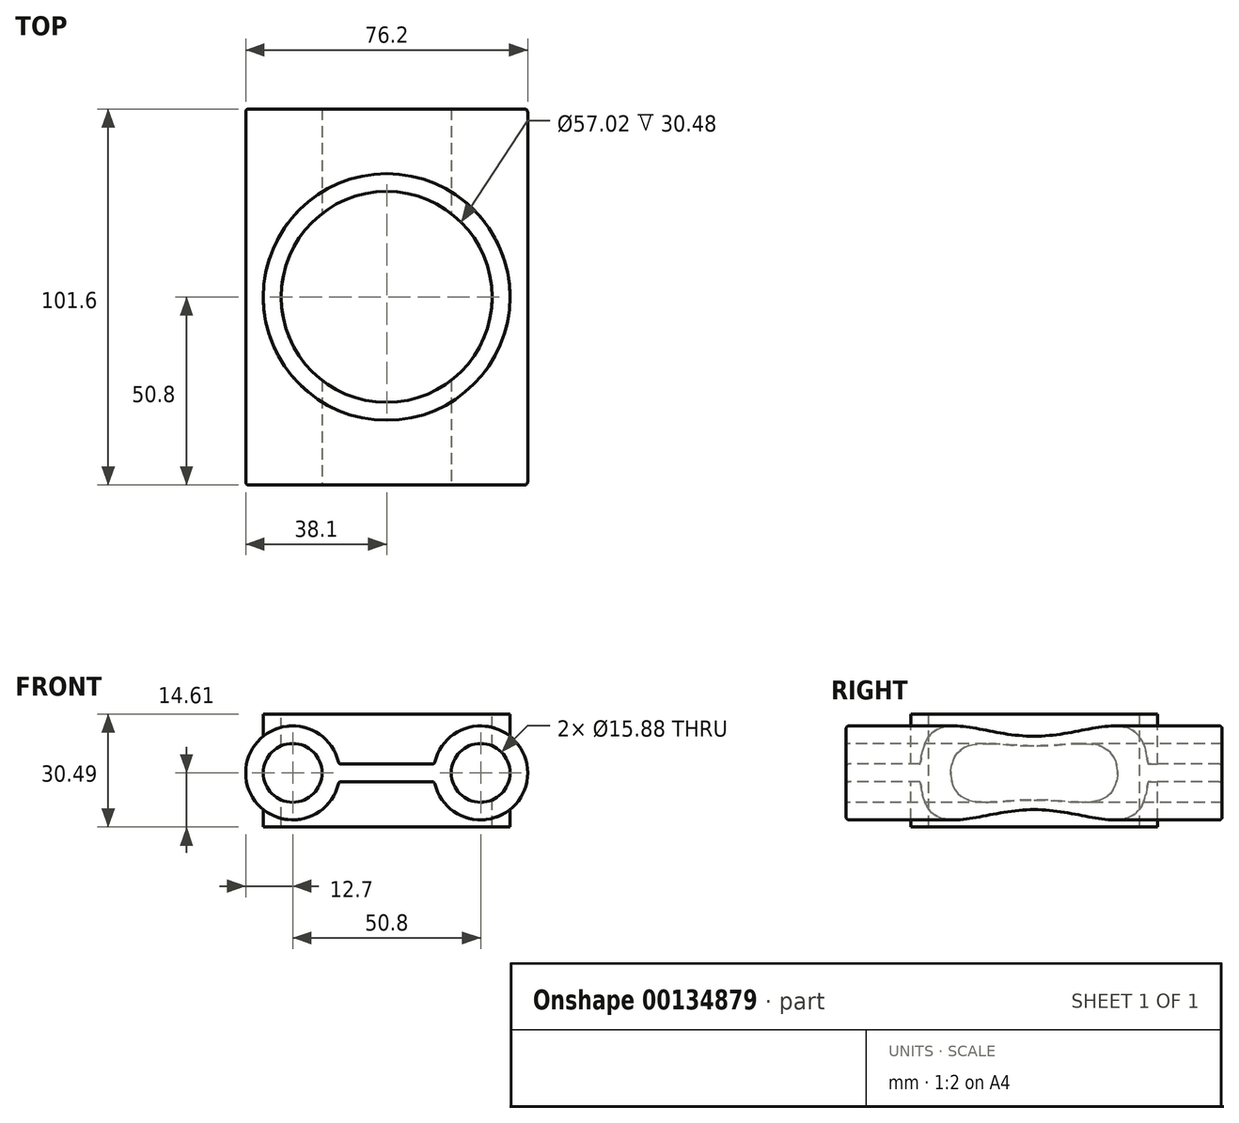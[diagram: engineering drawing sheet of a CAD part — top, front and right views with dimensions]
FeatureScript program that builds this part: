
annotation { "Feature Type Name" : "Feature", "Feature Type Description" : "" }
export const myFeature = defineFeature(function(context is Context, id is Id, definition is map)
    precondition{}
    {
        {
            var Q0;
            Q0=qCreatedBy(makeId("Front.planeOp"),FACE);
            var sketch = newSketch(context, id + "F0", { "sketchPlane" : qUnion([Q0])});
            skCircle(sketch, "E0", {"center": v(-25.4, 0) * mm, "radius": 7.94 * mm});
            skCircle(sketch, "E1", {"center": v(25.4, 0) * mm, "radius": 7.94 * mm});
            skLineSegment(sketch, "E2.bottom", {"start": v(-25.4, -12.7) * mm, "end": v(25.4, -12.7) * mm});
            skLineSegment(sketch, "E2.top", {"start": v(-25.4, 12.7) * mm, "end": v(25.4, 12.7) * mm});
            skLineSegment(sketch, "E3", {"start": v(0, 27.36) * mm, "end": v(0, -25.58) * mm, "construction": true});
            skArc(sketch, "E4.filletArc", {"start": v(-25.4, 12.7) * mm, "mid": v(-34.38, 8.98) * mm, "end": v(-38.1, 0) * mm});
            skLineSegment(sketch, "E5", {"start": v(41.42, 0) * mm, "end": v(-42.77, 0) * mm, "construction": true});
            skArc(sketch, "E6", {"start": v(25.4, -12.7) * mm, "mid": v(34.38, -8.98) * mm, "end": v(38.1, 0) * mm});
            skArc(sketch, "E7", {"start": v(25.4, 12.7) * mm, "mid": v(17.3, 9.79) * mm, "end": v(12.93, 2.38) * mm});
            skArc(sketch, "E8", {"start": v(-25.4, 12.7) * mm, "mid": v(-17.3, 9.79) * mm, "end": v(-12.93, 2.38) * mm});
            skLineSegment(sketch, "E9", {"start": v(12.93, 2.38) * mm, "end": v(-12.93, 2.38) * mm});
            skLineSegment(sketch, "E10", {"start": v(-12.93, -2.38) * mm, "end": v(12.93, -2.38) * mm});
            skArc(sketch, "E11.trimOffspring", {"start": v(-12.93, -2.38) * mm, "mid": v(-17.3, -9.79) * mm, "end": v(-25.4, -12.7) * mm});
            skArc(sketch, "E12.trimOffspring", {"start": v(12.93, -2.38) * mm, "mid": v(17.3, -9.79) * mm, "end": v(25.4, -12.7) * mm});
            skArc(sketch, "E13.trimOffspring", {"start": v(38.1, 0) * mm, "mid": v(34.38, 8.98) * mm, "end": v(25.4, 12.7) * mm});
            skArc(sketch, "E14.trimOffspring", {"start": v(-38.1, 0) * mm, "mid": v(-34.38, -8.98) * mm, "end": v(-25.4, -12.7) * mm});
            skLineSegment(sketch, "E15", {"start": v(-33.34, 24.61) * mm, "end": v(-33.34, -18.67) * mm, "construction": true});
            skSolve(sketch);
        }
        {
            var Q0;
            Q0=makeQuery(id+"F0.imprint","IMPRINT",FACE,{"disambiguationData":[TD([[makeQuery(id+"F0.imprint","IMPRINT",EDGE,{"derivedFrom":sQuery(id+"F0.wireOp",EDGE,"E0")}),-1.0]])]});
            var Q1;
            Q1=makeQuery(id+"F0.imprint","IMPRINT",FACE,{"disambiguationData":[TD([[makeQuery(id+"F0.imprint","IMPRINT",EDGE,{"derivedFrom":sQuery(id+"F0.wireOp",EDGE,"E0")}),1.0]])]});
            var Q2;
            Q2=makeQuery(id+"F0.imprint","IMPRINT",FACE,{"disambiguationData":[TD([[makeQuery(id+"F0.imprint","IMPRINT",EDGE,{"derivedFrom":sQuery(id+"F0.wireOp",EDGE,"E1")}),1.0]])]});
            extrude(context, id + "F1", {"entities" : qUnion([Q0, Q1, Q2]), "depth" : 101.6 * mm, "symmetric" : true});
        }
        {
            var Q0;
            Q0=qCreatedBy(makeId("Top.planeOp"),FACE);
            cPlane(context, id + "F2", {"entities" : qUnion([Q0]), "cplaneType" : CPlaneType.OFFSET, "offset" : 15.88 * mm, "width" : 152.4 * mm, "height" : 152.4 * mm});
        }
        {
            var Q0;
            Q0=qCreatedBy(makeId("Top.planeOp"),FACE);
            cPlane(context, id + "F3", {"entities" : qUnion([Q0]), "cplaneType" : CPlaneType.OFFSET, "offset" : 11.43 * mm, "oppositeDirection" : true, "width" : 152.4 * mm, "height" : 152.4 * mm});
        }
        {
            var Q0;
            Q0=qCreatedBy(id+"F2.planeOp",FACE);
            var sketch = newSketch(context, id + "F4", { "sketchPlane" : qUnion([Q0])});
            skCircle(sketch, "E16", {"center": v(0, 0) * mm, "radius": 33.34 * mm});
            skSolve(sketch);
        }
        {
            var Q0;
            Q0=qCreatedBy(id+"F3.planeOp",FACE);
            var sketch = newSketch(context, id + "F5", { "sketchPlane" : qUnion([Q0])});
            skLineSegment(sketch, "E17", {"start": v(0, -28.42) * mm, "end": v(0, -28.42) * mm, "construction": true});
            skPoint(sketch, "E17.startSnap0", {"position": v(0, -26.34) * mm});
            skPoint(sketch, "E17.endSnap0", {"position": v(0, -26.34) * mm});
            skLineSegment(sketch, "E18", {"start": v(0, -36.42) * mm, "end": v(0, 31.61) * mm, "construction": true});
            skCircle(sketch, "E19", {"center": v(0, 0) * mm, "radius": 27.94 * mm});
            skCircle(sketch, "E20", {"center": v(0, 0) * mm, "radius": 22.23 * mm});
            skSolve(sketch);
        }
        {
            var Q0;
            Q0=qCreatedBy(makeId("Front.planeOp"),FACE);
            var sketch = newSketch(context, id + "F6", { "sketchPlane" : qUnion([Q0])});
            skCircle(sketch, "E21", {"center": v(-25.4, 0) * mm, "radius": 7.94 * mm});
            skCircle(sketch, "E22", {"center": v(25.4, 0) * mm, "radius": 7.94 * mm});
            skSolve(sketch);
        }
        {
            var Q0;
            Q0=makeQuery(id+"F1.opExtrude","CAP_FACE",FACE,{"disambiguationData":[OSD([sQuery(id+"F0.wireOp",EDGE,"E0"),sQuery(id+"F0.wireOp",EDGE,"E1"),sQuery(id+"F0.wireOp",EDGE,"E4.filletArc"),sQuery(id+"F0.wireOp",EDGE,"E6"),sQuery(id+"F0.wireOp",EDGE,"E7"),sQuery(id+"F0.wireOp",EDGE,"E8"),sQuery(id+"F0.wireOp",EDGE,"E9"),sQuery(id+"F0.wireOp",EDGE,"E10"),sQuery(id+"F0.wireOp",EDGE,"E11.trimOffspring"),sQuery(id+"F0.wireOp",EDGE,"E12.trimOffspring"),sQuery(id+"F0.wireOp",EDGE,"56LLjDPh-25kw-j5da-6pGc-QQXyOrlAbZft"),sQuery(id+"F0.wireOp",EDGE,"nkBVuMIO-VIts-mmgG-adj7-daovQ4xWU2gD"),sQuery(id+"F0.wireOp",EDGE,"z16tnCEl-DL2h-uVAb-m06f-pflpMNFIArZW"),sQuery(id+"F0.wireOp",EDGE,"0xnEmYim-vQBw-8N55-9MmZ-LrTOjcDv7Glw"),sQuery(id+"F0.wireOp",EDGE,"68f398ec-cf93-4add-bcc9-37bf96ad6e88"),sQuery(id+"F0.wireOp",EDGE,"e56ac5f7-e3d4-4c3f-b5e2-56972c4acdce"),sQuery(id+"F0.wireOp",EDGE,"E13.trimOffspring"),sQuery(id+"F0.wireOp",EDGE,"E14.trimOffspring")])],"isStart":false});
            var Q1;
            Q1=makeQuery(id+"F1.opExtrude","CAP_EDGE",EDGE,{"disambiguationData":[OSD([sQuery(id+"F0.wireOp",EDGE,"E1")])],"isStart":true});
            var Q2;
            Q2=makeQuery(id+"F1.opExtrude","CAP_EDGE",EDGE,{"disambiguationData":[OSD([sQuery(id+"F0.wireOp",EDGE,"E0")])],"isStart":true});
            var Q3;
            Q3=makeQuery(id+"F1.opExtrude","CAP_FACE",FACE,{"disambiguationData":[OSD([sQuery(id+"F0.wireOp",EDGE,"E0"),sQuery(id+"F0.wireOp",EDGE,"E1"),sQuery(id+"F0.wireOp",EDGE,"E4.filletArc"),sQuery(id+"F0.wireOp",EDGE,"E6"),sQuery(id+"F0.wireOp",EDGE,"E7"),sQuery(id+"F0.wireOp",EDGE,"E8"),sQuery(id+"F0.wireOp",EDGE,"E9"),sQuery(id+"F0.wireOp",EDGE,"E10"),sQuery(id+"F0.wireOp",EDGE,"E11.trimOffspring"),sQuery(id+"F0.wireOp",EDGE,"E12.trimOffspring"),sQuery(id+"F0.wireOp",EDGE,"56LLjDPh-25kw-j5da-6pGc-QQXyOrlAbZft"),sQuery(id+"F0.wireOp",EDGE,"nkBVuMIO-VIts-mmgG-adj7-daovQ4xWU2gD"),sQuery(id+"F0.wireOp",EDGE,"z16tnCEl-DL2h-uVAb-m06f-pflpMNFIArZW"),sQuery(id+"F0.wireOp",EDGE,"0xnEmYim-vQBw-8N55-9MmZ-LrTOjcDv7Glw"),sQuery(id+"F0.wireOp",EDGE,"68f398ec-cf93-4add-bcc9-37bf96ad6e88"),sQuery(id+"F0.wireOp",EDGE,"e56ac5f7-e3d4-4c3f-b5e2-56972c4acdce"),sQuery(id+"F0.wireOp",EDGE,"E13.trimOffspring"),sQuery(id+"F0.wireOp",EDGE,"E14.trimOffspring")])],"isStart":true});
            var Q4;
            {var subQ0=sQuery(id+"F0.wireOp",EDGE,"E14.trimOffspring");var subQ1=sQuery(id+"F0.wireOp",EDGE,"E12.trimOffspring");var subQ2=sQuery(id+"F0.wireOp",EDGE,"E11.trimOffspring");var subQ3=sQuery(id+"F0.wireOp",EDGE,"E10");var subQ4=sQuery(id+"F0.wireOp",EDGE,"E6");Q4=makeQuery(id+"Fc4ntuCPbaOE7TT_1.boolean.opBoolean","INTERSECT",EDGE,{"derivedFrom":[makeQuery(id+"FMdS09tuQhoFYWg_1.boolean.opBoolean","SPLIT",FACE,{"disambiguationData":[TD([makeQuery(id+"F1.opExtrude","CAP_FACE",FACE,{"disambiguationData":[OSD([sQuery(id+"F0.wireOp",EDGE,"E0"),sQuery(id+"F0.wireOp",EDGE,"E1"),sQuery(id+"F0.wireOp",EDGE,"E4.filletArc"),subQ4,sQuery(id+"F0.wireOp",EDGE,"E7"),sQuery(id+"F0.wireOp",EDGE,"E8"),sQuery(id+"F0.wireOp",EDGE,"E9"),subQ3,subQ2,subQ1,sQuery(id+"F0.wireOp",EDGE,"56LLjDPh-25kw-j5da-6pGc-QQXyOrlAbZft"),sQuery(id+"F0.wireOp",EDGE,"nkBVuMIO-VIts-mmgG-adj7-daovQ4xWU2gD"),sQuery(id+"F0.wireOp",EDGE,"z16tnCEl-DL2h-uVAb-m06f-pflpMNFIArZW"),sQuery(id+"F0.wireOp",EDGE,"0xnEmYim-vQBw-8N55-9MmZ-LrTOjcDv7Glw"),sQuery(id+"F0.wireOp",EDGE,"68f398ec-cf93-4add-bcc9-37bf96ad6e88"),sQuery(id+"F0.wireOp",EDGE,"e56ac5f7-e3d4-4c3f-b5e2-56972c4acdce"),sQuery(id+"F0.wireOp",EDGE,"E13.trimOffspring"),subQ0])],"isStart":true})])],"derivedFrom":makeQuery(id+"F1.opExtrude","SWEPT_FACE",FACE,{"disambiguationData":[OSD([subQ3])]})}),makeQuery(id+"Fc4ntuCPbaOE7TT_1.opExtrude","SWEPT_FACE",FACE,{"disambiguationData":[OSD([sQuery(id+"F5.wireOp",EDGE,"E19")])]})]});}
            var Q5;
            {var subQ7=sQuery(id+"F0.wireOp",EDGE,"nkBVuMIO-VIts-mmgG-adj7-daovQ4xWU2gD");var subQ9=sQuery(id+"F0.wireOp",EDGE,"E12.trimOffspring");var subQ14=sQuery(id+"F0.wireOp",EDGE,"E6");Q5=makeQuery(id+"Fc4ntuCPbaOE7TT_1.boolean.opBoolean","INTERSECT",EDGE,{"disambiguationData":[OD(0.0)],"derivedFrom":[makeQuery(id+"FMdS09tuQhoFYWg_1.boolean.opBoolean","SPLIT",FACE,{"disambiguationData":[TD([makeQuery(id+"F1.opExtrude","SWEPT_FACE",FACE,{"disambiguationData":[OSD([subQ7])]})])],"derivedFrom":makeQuery(id+"F1.opExtrude","SWEPT_FACE",FACE,{"disambiguationData":[OSD([subQ14,subQ9])]})}),makeQuery(id+"Fc4ntuCPbaOE7TT_1.opExtrude","SWEPT_FACE",FACE,{"disambiguationData":[OSD([sQuery(id+"F5.wireOp",EDGE,"E19")])]})]});}
            var Q6;
            {var subQ0=sQuery(id+"F0.wireOp",EDGE,"0xnEmYim-vQBw-8N55-9MmZ-LrTOjcDv7Glw");var subQ1=sQuery(id+"F0.wireOp",EDGE,"E14.trimOffspring");var subQ9=sQuery(id+"F0.wireOp",EDGE,"E11.trimOffspring");Q6=makeQuery(id+"Fc4ntuCPbaOE7TT_1.boolean.opBoolean","INTERSECT",EDGE,{"disambiguationData":[OD(0.0)],"derivedFrom":[makeQuery(id+"FMdS09tuQhoFYWg_1.boolean.opBoolean","SPLIT",FACE,{"disambiguationData":[TD([makeQuery(id+"F1.opExtrude","SWEPT_FACE",FACE,{"disambiguationData":[OSD([subQ0])]})])],"derivedFrom":makeQuery(id+"F1.opExtrude","SWEPT_FACE",FACE,{"disambiguationData":[OSD([subQ9,subQ1])]})}),makeQuery(id+"Fc4ntuCPbaOE7TT_1.opExtrude","SWEPT_FACE",FACE,{"disambiguationData":[OSD([sQuery(id+"F5.wireOp",EDGE,"E19")])]})]});}
            var Q7;
            {var subQ7=sQuery(id+"F0.wireOp",EDGE,"nkBVuMIO-VIts-mmgG-adj7-daovQ4xWU2gD");var subQ9=sQuery(id+"F0.wireOp",EDGE,"E12.trimOffspring");var subQ14=sQuery(id+"F0.wireOp",EDGE,"E6");Q7=makeQuery(id+"Fc4ntuCPbaOE7TT_1.boolean.opBoolean","INTERSECT",EDGE,{"disambiguationData":[OD(1.0)],"derivedFrom":[makeQuery(id+"FMdS09tuQhoFYWg_1.boolean.opBoolean","SPLIT",FACE,{"disambiguationData":[TD([makeQuery(id+"F1.opExtrude","SWEPT_FACE",FACE,{"disambiguationData":[OSD([subQ7])]})])],"derivedFrom":makeQuery(id+"F1.opExtrude","SWEPT_FACE",FACE,{"disambiguationData":[OSD([subQ14,subQ9])]})}),makeQuery(id+"Fc4ntuCPbaOE7TT_1.opExtrude","SWEPT_FACE",FACE,{"disambiguationData":[OSD([sQuery(id+"F5.wireOp",EDGE,"E19")])]})]});}
            var Q8;
            {var subQ0=sQuery(id+"F0.wireOp",EDGE,"E14.trimOffspring");var subQ1=sQuery(id+"F0.wireOp",EDGE,"E12.trimOffspring");var subQ2=sQuery(id+"F0.wireOp",EDGE,"E11.trimOffspring");var subQ3=sQuery(id+"F0.wireOp",EDGE,"E10");var subQ4=sQuery(id+"F0.wireOp",EDGE,"E6");Q8=makeQuery(id+"Fc4ntuCPbaOE7TT_1.boolean.opBoolean","INTERSECT",EDGE,{"derivedFrom":[makeQuery(id+"FMdS09tuQhoFYWg_1.boolean.opBoolean","SPLIT",FACE,{"disambiguationData":[TD([makeQuery(id+"F1.opExtrude","CAP_FACE",FACE,{"disambiguationData":[OSD([sQuery(id+"F0.wireOp",EDGE,"E0"),sQuery(id+"F0.wireOp",EDGE,"E1"),sQuery(id+"F0.wireOp",EDGE,"E4.filletArc"),subQ4,sQuery(id+"F0.wireOp",EDGE,"E7"),sQuery(id+"F0.wireOp",EDGE,"E8"),sQuery(id+"F0.wireOp",EDGE,"E9"),subQ3,subQ2,subQ1,sQuery(id+"F0.wireOp",EDGE,"56LLjDPh-25kw-j5da-6pGc-QQXyOrlAbZft"),sQuery(id+"F0.wireOp",EDGE,"nkBVuMIO-VIts-mmgG-adj7-daovQ4xWU2gD"),sQuery(id+"F0.wireOp",EDGE,"z16tnCEl-DL2h-uVAb-m06f-pflpMNFIArZW"),sQuery(id+"F0.wireOp",EDGE,"0xnEmYim-vQBw-8N55-9MmZ-LrTOjcDv7Glw"),sQuery(id+"F0.wireOp",EDGE,"68f398ec-cf93-4add-bcc9-37bf96ad6e88"),sQuery(id+"F0.wireOp",EDGE,"e56ac5f7-e3d4-4c3f-b5e2-56972c4acdce"),sQuery(id+"F0.wireOp",EDGE,"E13.trimOffspring"),subQ0])],"isStart":false})])],"derivedFrom":makeQuery(id+"F1.opExtrude","SWEPT_FACE",FACE,{"disambiguationData":[OSD([subQ3])]})}),makeQuery(id+"Fc4ntuCPbaOE7TT_1.opExtrude","SWEPT_FACE",FACE,{"disambiguationData":[OSD([sQuery(id+"F5.wireOp",EDGE,"E19")])]})]});}
            var Q9;
            {var subQ0=sQuery(id+"F0.wireOp",EDGE,"0xnEmYim-vQBw-8N55-9MmZ-LrTOjcDv7Glw");var subQ1=sQuery(id+"F0.wireOp",EDGE,"E14.trimOffspring");var subQ9=sQuery(id+"F0.wireOp",EDGE,"E11.trimOffspring");Q9=makeQuery(id+"Fc4ntuCPbaOE7TT_1.boolean.opBoolean","INTERSECT",EDGE,{"disambiguationData":[OD(1.0)],"derivedFrom":[makeQuery(id+"FMdS09tuQhoFYWg_1.boolean.opBoolean","SPLIT",FACE,{"disambiguationData":[TD([makeQuery(id+"F1.opExtrude","SWEPT_FACE",FACE,{"disambiguationData":[OSD([subQ0])]})])],"derivedFrom":makeQuery(id+"F1.opExtrude","SWEPT_FACE",FACE,{"disambiguationData":[OSD([subQ9,subQ1])]})}),makeQuery(id+"Fc4ntuCPbaOE7TT_1.opExtrude","SWEPT_FACE",FACE,{"disambiguationData":[OSD([sQuery(id+"F5.wireOp",EDGE,"E19")])]})]});}
            var Q10;
            Q10=makeQuery(id+"FTNQrZDtOkg16al_1.opExtrude","TWEAK_EDGE",EDGE,{"disambiguationData":[OD(0.0)],"derivedFrom":[makeQuery(id+"F1.opExtrude","SWEPT_FACE",FACE,{"disambiguationData":[OSD([sQuery(id+"F0.wireOp",EDGE,"E9")])]}),makeQuery(id+"F4.imprint","IMPRINT",EDGE,{"derivedFrom":sQuery(id+"F4.wireOp",EDGE,"E16")})]});
            var Q11;
            Q11=makeQuery(id+"FTNQrZDtOkg16al_1.opExtrude","TWEAK_EDGE",EDGE,{"derivedFrom":[makeQuery(id+"F1.opExtrude","SWEPT_FACE",FACE,{"disambiguationData":[OSD([sQuery(id+"F0.wireOp",EDGE,"56LLjDPh-25kw-j5da-6pGc-QQXyOrlAbZft")])]}),makeQuery(id+"F4.imprint","IMPRINT",EDGE,{"derivedFrom":sQuery(id+"F4.wireOp",EDGE,"E16")})]});
            var Q12;
            Q12=makeQuery(id+"FTNQrZDtOkg16al_1.opExtrude","TWEAK_EDGE",EDGE,{"derivedFrom":[makeQuery(id+"F1.opExtrude","SWEPT_FACE",FACE,{"disambiguationData":[OSD([sQuery(id+"F0.wireOp",EDGE,"z16tnCEl-DL2h-uVAb-m06f-pflpMNFIArZW")])]}),makeQuery(id+"F4.imprint","IMPRINT",EDGE,{"derivedFrom":sQuery(id+"F4.wireOp",EDGE,"E16")})]});
            var Q13;
            Q13=makeQuery(id+"FTNQrZDtOkg16al_1.opExtrude","TWEAK_EDGE",EDGE,{"disambiguationData":[OD(1.0)],"derivedFrom":[makeQuery(id+"F1.opExtrude","SWEPT_FACE",FACE,{"disambiguationData":[OSD([sQuery(id+"F0.wireOp",EDGE,"E9")])]}),makeQuery(id+"F4.imprint","IMPRINT",EDGE,{"derivedFrom":sQuery(id+"F4.wireOp",EDGE,"E16")})]});
            var Q14;
            Q14=makeQuery(id+"F1.opExtrude","SWEPT_EDGE",EDGE,{"disambiguationData":[OSD([sQuery(id+"F0.wireOp",EDGE,"E6"),sQuery(id+"F0.wireOp",EDGE,"nkBVuMIO-VIts-mmgG-adj7-daovQ4xWU2gD")])]});
            var Q15;
            Q15=makeQuery(id+"F1.opExtrude","SWEPT_EDGE",EDGE,{"disambiguationData":[OSD([sQuery(id+"F0.wireOp",EDGE,"0xnEmYim-vQBw-8N55-9MmZ-LrTOjcDv7Glw"),sQuery(id+"F0.wireOp",EDGE,"E14.trimOffspring")])]});
            var Q16;
            {var subQ0=sQuery(id+"F0.wireOp",EDGE,"E14.trimOffspring");var subQ1=sQuery(id+"F0.wireOp",EDGE,"E11.trimOffspring");var subQ2=sQuery(id+"F0.wireOp",EDGE,"E10");Q16=makeQuery(id+"FMdS09tuQhoFYWg_1.boolean.opBoolean","SPLIT",EDGE,{"disambiguationData":[TD([makeQuery(id+"F1.opExtrude","CAP_FACE",FACE,{"disambiguationData":[OSD([sQuery(id+"F0.wireOp",EDGE,"E0"),sQuery(id+"F0.wireOp",EDGE,"E1"),sQuery(id+"F0.wireOp",EDGE,"E4.filletArc"),sQuery(id+"F0.wireOp",EDGE,"E6"),sQuery(id+"F0.wireOp",EDGE,"E7"),sQuery(id+"F0.wireOp",EDGE,"E8"),sQuery(id+"F0.wireOp",EDGE,"E9"),subQ2,subQ1,sQuery(id+"F0.wireOp",EDGE,"E12.trimOffspring"),sQuery(id+"F0.wireOp",EDGE,"56LLjDPh-25kw-j5da-6pGc-QQXyOrlAbZft"),sQuery(id+"F0.wireOp",EDGE,"nkBVuMIO-VIts-mmgG-adj7-daovQ4xWU2gD"),sQuery(id+"F0.wireOp",EDGE,"z16tnCEl-DL2h-uVAb-m06f-pflpMNFIArZW"),sQuery(id+"F0.wireOp",EDGE,"0xnEmYim-vQBw-8N55-9MmZ-LrTOjcDv7Glw"),sQuery(id+"F0.wireOp",EDGE,"68f398ec-cf93-4add-bcc9-37bf96ad6e88"),sQuery(id+"F0.wireOp",EDGE,"e56ac5f7-e3d4-4c3f-b5e2-56972c4acdce"),sQuery(id+"F0.wireOp",EDGE,"E13.trimOffspring"),subQ0])],"isStart":true})])],"derivedFrom":makeQuery(id+"F1.opExtrude","SWEPT_EDGE",EDGE,{"disambiguationData":[OSD([subQ2,subQ1])]})});}
            var Q17;
            {var subQ0=sQuery(id+"F0.wireOp",EDGE,"E14.trimOffspring");var subQ1=sQuery(id+"F0.wireOp",EDGE,"E11.trimOffspring");var subQ2=sQuery(id+"F0.wireOp",EDGE,"E10");Q17=makeQuery(id+"FMdS09tuQhoFYWg_1.boolean.opBoolean","SPLIT",EDGE,{"disambiguationData":[TD([makeQuery(id+"F1.opExtrude","CAP_FACE",FACE,{"disambiguationData":[OSD([sQuery(id+"F0.wireOp",EDGE,"E0"),sQuery(id+"F0.wireOp",EDGE,"E1"),sQuery(id+"F0.wireOp",EDGE,"E4.filletArc"),sQuery(id+"F0.wireOp",EDGE,"E6"),sQuery(id+"F0.wireOp",EDGE,"E7"),sQuery(id+"F0.wireOp",EDGE,"E8"),sQuery(id+"F0.wireOp",EDGE,"E9"),subQ2,subQ1,sQuery(id+"F0.wireOp",EDGE,"E12.trimOffspring"),sQuery(id+"F0.wireOp",EDGE,"56LLjDPh-25kw-j5da-6pGc-QQXyOrlAbZft"),sQuery(id+"F0.wireOp",EDGE,"nkBVuMIO-VIts-mmgG-adj7-daovQ4xWU2gD"),sQuery(id+"F0.wireOp",EDGE,"z16tnCEl-DL2h-uVAb-m06f-pflpMNFIArZW"),sQuery(id+"F0.wireOp",EDGE,"0xnEmYim-vQBw-8N55-9MmZ-LrTOjcDv7Glw"),sQuery(id+"F0.wireOp",EDGE,"68f398ec-cf93-4add-bcc9-37bf96ad6e88"),sQuery(id+"F0.wireOp",EDGE,"e56ac5f7-e3d4-4c3f-b5e2-56972c4acdce"),sQuery(id+"F0.wireOp",EDGE,"E13.trimOffspring"),subQ0])],"isStart":false})])],"derivedFrom":makeQuery(id+"F1.opExtrude","SWEPT_EDGE",EDGE,{"disambiguationData":[OSD([subQ2,subQ1])]})});}
            var Q18;
            {var subQ0=sQuery(id+"F0.wireOp",EDGE,"E12.trimOffspring");var subQ1=sQuery(id+"F0.wireOp",EDGE,"E10");var subQ2=sQuery(id+"F0.wireOp",EDGE,"E6");Q18=makeQuery(id+"FMdS09tuQhoFYWg_1.boolean.opBoolean","SPLIT",EDGE,{"disambiguationData":[TD([makeQuery(id+"F1.opExtrude","CAP_FACE",FACE,{"disambiguationData":[OSD([sQuery(id+"F0.wireOp",EDGE,"E0"),sQuery(id+"F0.wireOp",EDGE,"E1"),sQuery(id+"F0.wireOp",EDGE,"E4.filletArc"),subQ2,sQuery(id+"F0.wireOp",EDGE,"E7"),sQuery(id+"F0.wireOp",EDGE,"E8"),sQuery(id+"F0.wireOp",EDGE,"E9"),subQ1,sQuery(id+"F0.wireOp",EDGE,"E11.trimOffspring"),subQ0,sQuery(id+"F0.wireOp",EDGE,"56LLjDPh-25kw-j5da-6pGc-QQXyOrlAbZft"),sQuery(id+"F0.wireOp",EDGE,"nkBVuMIO-VIts-mmgG-adj7-daovQ4xWU2gD"),sQuery(id+"F0.wireOp",EDGE,"z16tnCEl-DL2h-uVAb-m06f-pflpMNFIArZW"),sQuery(id+"F0.wireOp",EDGE,"0xnEmYim-vQBw-8N55-9MmZ-LrTOjcDv7Glw"),sQuery(id+"F0.wireOp",EDGE,"68f398ec-cf93-4add-bcc9-37bf96ad6e88"),sQuery(id+"F0.wireOp",EDGE,"e56ac5f7-e3d4-4c3f-b5e2-56972c4acdce"),sQuery(id+"F0.wireOp",EDGE,"E13.trimOffspring"),sQuery(id+"F0.wireOp",EDGE,"E14.trimOffspring")])],"isStart":true})])],"derivedFrom":makeQuery(id+"F1.opExtrude","SWEPT_EDGE",EDGE,{"disambiguationData":[OSD([subQ1,subQ0])]})});}
            var Q19;
            {var subQ0=sQuery(id+"F0.wireOp",EDGE,"E12.trimOffspring");var subQ1=sQuery(id+"F0.wireOp",EDGE,"E10");var subQ2=sQuery(id+"F0.wireOp",EDGE,"E6");Q19=makeQuery(id+"FMdS09tuQhoFYWg_1.boolean.opBoolean","SPLIT",EDGE,{"disambiguationData":[TD([makeQuery(id+"F1.opExtrude","CAP_FACE",FACE,{"disambiguationData":[OSD([sQuery(id+"F0.wireOp",EDGE,"E0"),sQuery(id+"F0.wireOp",EDGE,"E1"),sQuery(id+"F0.wireOp",EDGE,"E4.filletArc"),subQ2,sQuery(id+"F0.wireOp",EDGE,"E7"),sQuery(id+"F0.wireOp",EDGE,"E8"),sQuery(id+"F0.wireOp",EDGE,"E9"),subQ1,sQuery(id+"F0.wireOp",EDGE,"E11.trimOffspring"),subQ0,sQuery(id+"F0.wireOp",EDGE,"56LLjDPh-25kw-j5da-6pGc-QQXyOrlAbZft"),sQuery(id+"F0.wireOp",EDGE,"nkBVuMIO-VIts-mmgG-adj7-daovQ4xWU2gD"),sQuery(id+"F0.wireOp",EDGE,"z16tnCEl-DL2h-uVAb-m06f-pflpMNFIArZW"),sQuery(id+"F0.wireOp",EDGE,"0xnEmYim-vQBw-8N55-9MmZ-LrTOjcDv7Glw"),sQuery(id+"F0.wireOp",EDGE,"68f398ec-cf93-4add-bcc9-37bf96ad6e88"),sQuery(id+"F0.wireOp",EDGE,"e56ac5f7-e3d4-4c3f-b5e2-56972c4acdce"),sQuery(id+"F0.wireOp",EDGE,"E13.trimOffspring"),sQuery(id+"F0.wireOp",EDGE,"E14.trimOffspring")])],"isStart":false})])],"derivedFrom":makeQuery(id+"F1.opExtrude","SWEPT_EDGE",EDGE,{"disambiguationData":[OSD([subQ1,subQ0])]})});}
            var Q20;
            {var subQ0=sQuery(id+"F0.wireOp",EDGE,"z16tnCEl-DL2h-uVAb-m06f-pflpMNFIArZW");var subQ1=sQuery(id+"F0.wireOp",EDGE,"E8");var subQ2=sQuery(id+"F0.wireOp",EDGE,"E4.filletArc");Q20=makeQuery(id+"FTNQrZDtOkg16al_1.boolean.opBoolean","SPLIT",EDGE,{"disambiguationData":[TD([makeQuery(id+"F1.opExtrude","CAP_FACE",FACE,{"disambiguationData":[OSD([sQuery(id+"F0.wireOp",EDGE,"E0"),sQuery(id+"F0.wireOp",EDGE,"E1"),subQ2,sQuery(id+"F0.wireOp",EDGE,"E6"),sQuery(id+"F0.wireOp",EDGE,"E7"),subQ1,sQuery(id+"F0.wireOp",EDGE,"E9"),sQuery(id+"F0.wireOp",EDGE,"E10"),sQuery(id+"F0.wireOp",EDGE,"E11.trimOffspring"),sQuery(id+"F0.wireOp",EDGE,"E12.trimOffspring"),sQuery(id+"F0.wireOp",EDGE,"56LLjDPh-25kw-j5da-6pGc-QQXyOrlAbZft"),sQuery(id+"F0.wireOp",EDGE,"nkBVuMIO-VIts-mmgG-adj7-daovQ4xWU2gD"),subQ0,sQuery(id+"F0.wireOp",EDGE,"0xnEmYim-vQBw-8N55-9MmZ-LrTOjcDv7Glw"),sQuery(id+"F0.wireOp",EDGE,"68f398ec-cf93-4add-bcc9-37bf96ad6e88"),sQuery(id+"F0.wireOp",EDGE,"e56ac5f7-e3d4-4c3f-b5e2-56972c4acdce"),sQuery(id+"F0.wireOp",EDGE,"E13.trimOffspring"),sQuery(id+"F0.wireOp",EDGE,"E14.trimOffspring")])],"isStart":false})])],"derivedFrom":makeQuery(id+"F1.opExtrude","SWEPT_EDGE",EDGE,{"disambiguationData":[OSD([subQ2,subQ0])]})});}
            var Q21;
            {var subQ0=sQuery(id+"F0.wireOp",EDGE,"z16tnCEl-DL2h-uVAb-m06f-pflpMNFIArZW");var subQ1=sQuery(id+"F0.wireOp",EDGE,"E8");var subQ2=sQuery(id+"F0.wireOp",EDGE,"E4.filletArc");Q21=makeQuery(id+"FTNQrZDtOkg16al_1.boolean.opBoolean","SPLIT",EDGE,{"disambiguationData":[TD([makeQuery(id+"F1.opExtrude","CAP_FACE",FACE,{"disambiguationData":[OSD([sQuery(id+"F0.wireOp",EDGE,"E0"),sQuery(id+"F0.wireOp",EDGE,"E1"),subQ2,sQuery(id+"F0.wireOp",EDGE,"E6"),sQuery(id+"F0.wireOp",EDGE,"E7"),subQ1,sQuery(id+"F0.wireOp",EDGE,"E9"),sQuery(id+"F0.wireOp",EDGE,"E10"),sQuery(id+"F0.wireOp",EDGE,"E11.trimOffspring"),sQuery(id+"F0.wireOp",EDGE,"E12.trimOffspring"),sQuery(id+"F0.wireOp",EDGE,"56LLjDPh-25kw-j5da-6pGc-QQXyOrlAbZft"),sQuery(id+"F0.wireOp",EDGE,"nkBVuMIO-VIts-mmgG-adj7-daovQ4xWU2gD"),subQ0,sQuery(id+"F0.wireOp",EDGE,"0xnEmYim-vQBw-8N55-9MmZ-LrTOjcDv7Glw"),sQuery(id+"F0.wireOp",EDGE,"68f398ec-cf93-4add-bcc9-37bf96ad6e88"),sQuery(id+"F0.wireOp",EDGE,"e56ac5f7-e3d4-4c3f-b5e2-56972c4acdce"),sQuery(id+"F0.wireOp",EDGE,"E13.trimOffspring"),sQuery(id+"F0.wireOp",EDGE,"E14.trimOffspring")])],"isStart":true})])],"derivedFrom":makeQuery(id+"F1.opExtrude","SWEPT_EDGE",EDGE,{"disambiguationData":[OSD([subQ2,subQ0])]})});}
            var Q22;
            {var subQ0=sQuery(id+"F0.wireOp",EDGE,"E9");var subQ1=sQuery(id+"F0.wireOp",EDGE,"E8");var subQ2=sQuery(id+"F0.wireOp",EDGE,"E4.filletArc");Q22=makeQuery(id+"FTNQrZDtOkg16al_1.boolean.opBoolean","SPLIT",EDGE,{"disambiguationData":[TD([makeQuery(id+"F1.opExtrude","CAP_FACE",FACE,{"disambiguationData":[OSD([sQuery(id+"F0.wireOp",EDGE,"E0"),sQuery(id+"F0.wireOp",EDGE,"E1"),subQ2,sQuery(id+"F0.wireOp",EDGE,"E6"),sQuery(id+"F0.wireOp",EDGE,"E7"),subQ1,subQ0,sQuery(id+"F0.wireOp",EDGE,"E10"),sQuery(id+"F0.wireOp",EDGE,"E11.trimOffspring"),sQuery(id+"F0.wireOp",EDGE,"E12.trimOffspring"),sQuery(id+"F0.wireOp",EDGE,"56LLjDPh-25kw-j5da-6pGc-QQXyOrlAbZft"),sQuery(id+"F0.wireOp",EDGE,"nkBVuMIO-VIts-mmgG-adj7-daovQ4xWU2gD"),sQuery(id+"F0.wireOp",EDGE,"z16tnCEl-DL2h-uVAb-m06f-pflpMNFIArZW"),sQuery(id+"F0.wireOp",EDGE,"0xnEmYim-vQBw-8N55-9MmZ-LrTOjcDv7Glw"),sQuery(id+"F0.wireOp",EDGE,"68f398ec-cf93-4add-bcc9-37bf96ad6e88"),sQuery(id+"F0.wireOp",EDGE,"e56ac5f7-e3d4-4c3f-b5e2-56972c4acdce"),sQuery(id+"F0.wireOp",EDGE,"E13.trimOffspring"),sQuery(id+"F0.wireOp",EDGE,"E14.trimOffspring")])],"isStart":true})])],"derivedFrom":makeQuery(id+"F1.opExtrude","SWEPT_EDGE",EDGE,{"disambiguationData":[OSD([subQ1,subQ0])]})});}
            var Q23;
            {var subQ0=sQuery(id+"F0.wireOp",EDGE,"E13.trimOffspring");var subQ1=sQuery(id+"F0.wireOp",EDGE,"E9");var subQ2=sQuery(id+"F0.wireOp",EDGE,"E7");Q23=makeQuery(id+"FTNQrZDtOkg16al_1.boolean.opBoolean","SPLIT",EDGE,{"disambiguationData":[TD([makeQuery(id+"F1.opExtrude","CAP_FACE",FACE,{"disambiguationData":[OSD([sQuery(id+"F0.wireOp",EDGE,"E0"),sQuery(id+"F0.wireOp",EDGE,"E1"),sQuery(id+"F0.wireOp",EDGE,"E4.filletArc"),sQuery(id+"F0.wireOp",EDGE,"E6"),subQ2,sQuery(id+"F0.wireOp",EDGE,"E8"),subQ1,sQuery(id+"F0.wireOp",EDGE,"E10"),sQuery(id+"F0.wireOp",EDGE,"E11.trimOffspring"),sQuery(id+"F0.wireOp",EDGE,"E12.trimOffspring"),sQuery(id+"F0.wireOp",EDGE,"56LLjDPh-25kw-j5da-6pGc-QQXyOrlAbZft"),sQuery(id+"F0.wireOp",EDGE,"nkBVuMIO-VIts-mmgG-adj7-daovQ4xWU2gD"),sQuery(id+"F0.wireOp",EDGE,"z16tnCEl-DL2h-uVAb-m06f-pflpMNFIArZW"),sQuery(id+"F0.wireOp",EDGE,"0xnEmYim-vQBw-8N55-9MmZ-LrTOjcDv7Glw"),sQuery(id+"F0.wireOp",EDGE,"68f398ec-cf93-4add-bcc9-37bf96ad6e88"),sQuery(id+"F0.wireOp",EDGE,"e56ac5f7-e3d4-4c3f-b5e2-56972c4acdce"),subQ0,sQuery(id+"F0.wireOp",EDGE,"E14.trimOffspring")])],"isStart":true})])],"derivedFrom":makeQuery(id+"F1.opExtrude","SWEPT_EDGE",EDGE,{"disambiguationData":[OSD([subQ2,subQ1])]})});}
            var Q24;
            {var subQ0=sQuery(id+"F0.wireOp",EDGE,"E13.trimOffspring");var subQ1=sQuery(id+"F0.wireOp",EDGE,"56LLjDPh-25kw-j5da-6pGc-QQXyOrlAbZft");var subQ2=sQuery(id+"F0.wireOp",EDGE,"E7");Q24=makeQuery(id+"FTNQrZDtOkg16al_1.boolean.opBoolean","SPLIT",EDGE,{"disambiguationData":[TD([makeQuery(id+"F1.opExtrude","CAP_FACE",FACE,{"disambiguationData":[OSD([sQuery(id+"F0.wireOp",EDGE,"E0"),sQuery(id+"F0.wireOp",EDGE,"E1"),sQuery(id+"F0.wireOp",EDGE,"E4.filletArc"),sQuery(id+"F0.wireOp",EDGE,"E6"),subQ2,sQuery(id+"F0.wireOp",EDGE,"E8"),sQuery(id+"F0.wireOp",EDGE,"E9"),sQuery(id+"F0.wireOp",EDGE,"E10"),sQuery(id+"F0.wireOp",EDGE,"E11.trimOffspring"),sQuery(id+"F0.wireOp",EDGE,"E12.trimOffspring"),subQ1,sQuery(id+"F0.wireOp",EDGE,"nkBVuMIO-VIts-mmgG-adj7-daovQ4xWU2gD"),sQuery(id+"F0.wireOp",EDGE,"z16tnCEl-DL2h-uVAb-m06f-pflpMNFIArZW"),sQuery(id+"F0.wireOp",EDGE,"0xnEmYim-vQBw-8N55-9MmZ-LrTOjcDv7Glw"),sQuery(id+"F0.wireOp",EDGE,"68f398ec-cf93-4add-bcc9-37bf96ad6e88"),sQuery(id+"F0.wireOp",EDGE,"e56ac5f7-e3d4-4c3f-b5e2-56972c4acdce"),subQ0,sQuery(id+"F0.wireOp",EDGE,"E14.trimOffspring")])],"isStart":true})])],"derivedFrom":makeQuery(id+"F1.opExtrude","SWEPT_EDGE",EDGE,{"disambiguationData":[OSD([subQ1,subQ0])]})});}
            var Q25;
            {var subQ0=sQuery(id+"F0.wireOp",EDGE,"E13.trimOffspring");var subQ1=sQuery(id+"F0.wireOp",EDGE,"56LLjDPh-25kw-j5da-6pGc-QQXyOrlAbZft");var subQ2=sQuery(id+"F0.wireOp",EDGE,"E7");Q25=makeQuery(id+"FTNQrZDtOkg16al_1.boolean.opBoolean","SPLIT",EDGE,{"disambiguationData":[TD([makeQuery(id+"F1.opExtrude","CAP_FACE",FACE,{"disambiguationData":[OSD([sQuery(id+"F0.wireOp",EDGE,"E0"),sQuery(id+"F0.wireOp",EDGE,"E1"),sQuery(id+"F0.wireOp",EDGE,"E4.filletArc"),sQuery(id+"F0.wireOp",EDGE,"E6"),subQ2,sQuery(id+"F0.wireOp",EDGE,"E8"),sQuery(id+"F0.wireOp",EDGE,"E9"),sQuery(id+"F0.wireOp",EDGE,"E10"),sQuery(id+"F0.wireOp",EDGE,"E11.trimOffspring"),sQuery(id+"F0.wireOp",EDGE,"E12.trimOffspring"),subQ1,sQuery(id+"F0.wireOp",EDGE,"nkBVuMIO-VIts-mmgG-adj7-daovQ4xWU2gD"),sQuery(id+"F0.wireOp",EDGE,"z16tnCEl-DL2h-uVAb-m06f-pflpMNFIArZW"),sQuery(id+"F0.wireOp",EDGE,"0xnEmYim-vQBw-8N55-9MmZ-LrTOjcDv7Glw"),sQuery(id+"F0.wireOp",EDGE,"68f398ec-cf93-4add-bcc9-37bf96ad6e88"),sQuery(id+"F0.wireOp",EDGE,"e56ac5f7-e3d4-4c3f-b5e2-56972c4acdce"),subQ0,sQuery(id+"F0.wireOp",EDGE,"E14.trimOffspring")])],"isStart":false})])],"derivedFrom":makeQuery(id+"F1.opExtrude","SWEPT_EDGE",EDGE,{"disambiguationData":[OSD([subQ1,subQ0])]})});}
            var Q26;
            Q26=makeQuery(id+"FTNQrZDtOkg16al_1.opExtrude","TWEAK_EDGE",EDGE,{"disambiguationData":[OD(1.0)],"derivedFrom":[makeQuery(id+"F1.opExtrude","SWEPT_FACE",FACE,{"disambiguationData":[OSD([sQuery(id+"F0.wireOp",EDGE,"E7"),sQuery(id+"F0.wireOp",EDGE,"E13.trimOffspring")])]}),makeQuery(id+"F4.imprint","IMPRINT",EDGE,{"derivedFrom":sQuery(id+"F4.wireOp",EDGE,"E16")})]});
            var Q27;
            Q27=makeQuery(id+"FTNQrZDtOkg16al_1.opExtrude","TWEAK_EDGE",EDGE,{"disambiguationData":[OD(1.0)],"derivedFrom":[makeQuery(id+"F1.opExtrude","SWEPT_FACE",FACE,{"disambiguationData":[OSD([sQuery(id+"F0.wireOp",EDGE,"E4.filletArc"),sQuery(id+"F0.wireOp",EDGE,"E8")])]}),makeQuery(id+"F4.imprint","IMPRINT",EDGE,{"derivedFrom":sQuery(id+"F4.wireOp",EDGE,"E16")})]});
            var Q28;
            Q28=makeQuery(id+"FTNQrZDtOkg16al_1.opExtrude","TWEAK_EDGE",EDGE,{"disambiguationData":[OD(0.0)],"derivedFrom":[makeQuery(id+"F1.opExtrude","SWEPT_FACE",FACE,{"disambiguationData":[OSD([sQuery(id+"F0.wireOp",EDGE,"E4.filletArc"),sQuery(id+"F0.wireOp",EDGE,"E8")])]}),makeQuery(id+"F4.imprint","IMPRINT",EDGE,{"derivedFrom":sQuery(id+"F4.wireOp",EDGE,"E16")})]});
            var Q29;
            Q29=makeQuery(id+"FTNQrZDtOkg16al_1.opExtrude","TWEAK_EDGE",EDGE,{"disambiguationData":[OD(0.0)],"derivedFrom":[makeQuery(id+"F1.opExtrude","SWEPT_FACE",FACE,{"disambiguationData":[OSD([sQuery(id+"F0.wireOp",EDGE,"E7"),sQuery(id+"F0.wireOp",EDGE,"E13.trimOffspring")])]}),makeQuery(id+"F4.imprint","IMPRINT",EDGE,{"derivedFrom":sQuery(id+"F4.wireOp",EDGE,"E16")})]});
            var Q30;
            {var subQ0=sQuery(id+"F0.wireOp",EDGE,"E13.trimOffspring");var subQ1=sQuery(id+"F0.wireOp",EDGE,"E9");var subQ2=sQuery(id+"F0.wireOp",EDGE,"E7");Q30=makeQuery(id+"FTNQrZDtOkg16al_1.boolean.opBoolean","SPLIT",EDGE,{"disambiguationData":[TD([makeQuery(id+"F1.opExtrude","CAP_FACE",FACE,{"disambiguationData":[OSD([sQuery(id+"F0.wireOp",EDGE,"E0"),sQuery(id+"F0.wireOp",EDGE,"E1"),sQuery(id+"F0.wireOp",EDGE,"E4.filletArc"),sQuery(id+"F0.wireOp",EDGE,"E6"),subQ2,sQuery(id+"F0.wireOp",EDGE,"E8"),subQ1,sQuery(id+"F0.wireOp",EDGE,"E10"),sQuery(id+"F0.wireOp",EDGE,"E11.trimOffspring"),sQuery(id+"F0.wireOp",EDGE,"E12.trimOffspring"),sQuery(id+"F0.wireOp",EDGE,"56LLjDPh-25kw-j5da-6pGc-QQXyOrlAbZft"),sQuery(id+"F0.wireOp",EDGE,"nkBVuMIO-VIts-mmgG-adj7-daovQ4xWU2gD"),sQuery(id+"F0.wireOp",EDGE,"z16tnCEl-DL2h-uVAb-m06f-pflpMNFIArZW"),sQuery(id+"F0.wireOp",EDGE,"0xnEmYim-vQBw-8N55-9MmZ-LrTOjcDv7Glw"),sQuery(id+"F0.wireOp",EDGE,"68f398ec-cf93-4add-bcc9-37bf96ad6e88"),sQuery(id+"F0.wireOp",EDGE,"e56ac5f7-e3d4-4c3f-b5e2-56972c4acdce"),subQ0,sQuery(id+"F0.wireOp",EDGE,"E14.trimOffspring")])],"isStart":false})])],"derivedFrom":makeQuery(id+"F1.opExtrude","SWEPT_EDGE",EDGE,{"disambiguationData":[OSD([subQ2,subQ1])]})});}
            var Q31;
            {var subQ0=sQuery(id+"F0.wireOp",EDGE,"E9");var subQ1=sQuery(id+"F0.wireOp",EDGE,"E8");var subQ2=sQuery(id+"F0.wireOp",EDGE,"E4.filletArc");Q31=makeQuery(id+"FTNQrZDtOkg16al_1.boolean.opBoolean","SPLIT",EDGE,{"disambiguationData":[TD([makeQuery(id+"F1.opExtrude","CAP_FACE",FACE,{"disambiguationData":[OSD([sQuery(id+"F0.wireOp",EDGE,"E0"),sQuery(id+"F0.wireOp",EDGE,"E1"),subQ2,sQuery(id+"F0.wireOp",EDGE,"E6"),sQuery(id+"F0.wireOp",EDGE,"E7"),subQ1,subQ0,sQuery(id+"F0.wireOp",EDGE,"E10"),sQuery(id+"F0.wireOp",EDGE,"E11.trimOffspring"),sQuery(id+"F0.wireOp",EDGE,"E12.trimOffspring"),sQuery(id+"F0.wireOp",EDGE,"56LLjDPh-25kw-j5da-6pGc-QQXyOrlAbZft"),sQuery(id+"F0.wireOp",EDGE,"nkBVuMIO-VIts-mmgG-adj7-daovQ4xWU2gD"),sQuery(id+"F0.wireOp",EDGE,"z16tnCEl-DL2h-uVAb-m06f-pflpMNFIArZW"),sQuery(id+"F0.wireOp",EDGE,"0xnEmYim-vQBw-8N55-9MmZ-LrTOjcDv7Glw"),sQuery(id+"F0.wireOp",EDGE,"68f398ec-cf93-4add-bcc9-37bf96ad6e88"),sQuery(id+"F0.wireOp",EDGE,"e56ac5f7-e3d4-4c3f-b5e2-56972c4acdce"),sQuery(id+"F0.wireOp",EDGE,"E13.trimOffspring"),sQuery(id+"F0.wireOp",EDGE,"E14.trimOffspring")])],"isStart":false})])],"derivedFrom":makeQuery(id+"F1.opExtrude","SWEPT_EDGE",EDGE,{"disambiguationData":[OSD([subQ1,subQ0])]})});}
            fillet(context, id + "F7", {"entities" : qUnion([Q0, Q1, Q2, Q3, Q4, Q5, Q6, Q7, Q8, Q9, Q10, Q11, Q12, Q13, Q14, Q15, Q16, Q17, Q18, Q19, Q20, Q21, Q22, Q23, Q24, Q25, Q26, Q27, Q28, Q29, Q30, Q31]), "radius" : 0.76 * mm, "tangentPropagation" : true, "allowEdgeOverflow" : false});
        }
        {
            var Q0;
            Q0=makeQuery(id+"F4.imprint","IMPRINT",FACE,{"disambiguationData":[TD([[makeQuery(id+"F4.imprint","IMPRINT",EDGE,{"derivedFrom":sQuery(id+"F4.wireOp",EDGE,"E16")}),1.0]])]});
            extrude(context, id + "F8", {"entities" : qUnion([Q0]), "operationType" : NewBodyOperationType.REMOVE, "endBound" : BoundingType.THROUGH_ALL, "oppositeDirection" : true, "depth" : 25.4 * mm});
        }
        {
            var Q0;
            Q0=qCreatedBy(id+"F2.planeOp",FACE);
            var sketch = newSketch(context, id + "F9", { "sketchPlane" : qUnion([Q0])});
            skArc(sketch, "E23.0", {"start": v(-13.05, 30.68) * mm, "mid": v(-33.34, 0) * mm, "end": v(-13.05, -30.68) * mm});
            skArc(sketch, "E23.1", {"start": v(12.31, -30.98) * mm, "mid": v(0, -33.34) * mm, "end": v(-12.31, -30.98) * mm});
            skArc(sketch, "E23.2", {"start": v(13.05, -30.68) * mm, "mid": v(33.34, 0) * mm, "end": v(13.05, 30.68) * mm});
            skArc(sketch, "E23.3", {"start": v(-12.31, 30.98) * mm, "mid": v(0, 33.34) * mm, "end": v(12.31, 30.98) * mm});
            skArc(sketch, "E23.4", {"start": v(-12.31, 30.98) * mm, "mid": v(-12.68, 30.83) * mm, "end": v(-13.05, 30.68) * mm});
            skArc(sketch, "E23.5", {"start": v(13.05, 30.68) * mm, "mid": v(12.68, 30.83) * mm, "end": v(12.31, 30.98) * mm});
            skArc(sketch, "E23.6", {"start": v(12.31, -30.98) * mm, "mid": v(12.68, -30.83) * mm, "end": v(13.05, -30.68) * mm});
            skArc(sketch, "E23.7", {"start": v(-13.05, -30.68) * mm, "mid": v(-12.68, -30.83) * mm, "end": v(-12.31, -30.98) * mm});
            skCircle(sketch, "E24", {"center": v(0, 0) * mm, "radius": 28.51 * mm});
            skSolve(sketch);
        }
        {
            var Q0;
            Q0=makeQuery(id+"F9.imprint","IMPRINT",FACE,{"disambiguationData":[TD([[makeQuery(id+"F9.imprint","IMPRINT",EDGE,{"derivedFrom":sQuery(id+"F9.wireOp",EDGE,"E23.0")}),1.0]])]});
            extrude(context, id + "F10", {"entities" : qUnion([Q0]), "operationType" : NewBodyOperationType.ADD, "oppositeDirection" : true, "depth" : 30.48 * mm});
        }
        {
            var Q0;
            Q0 = qSketchRegion(id + "F6", true);
            extrude(context, id + "F11", {"entities" : qUnion([Q0]), "operationType" : NewBodyOperationType.REMOVE, "oppositeDirection" : true, "depth" : 101.6 * mm, "symmetric" : true});
        }
    });
